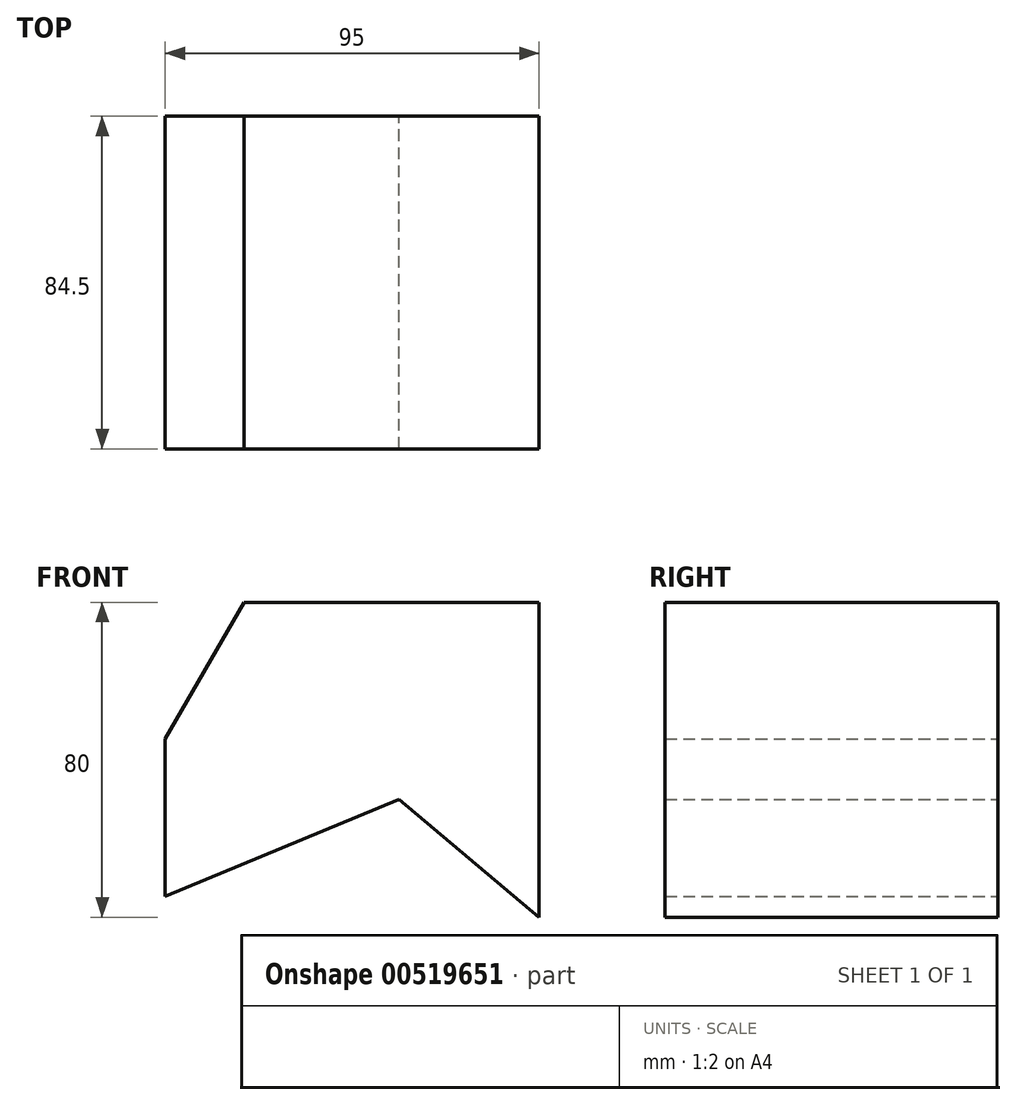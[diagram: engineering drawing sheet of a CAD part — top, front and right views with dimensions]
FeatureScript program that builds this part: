
annotation { "Feature Type Name" : "Feature", "Feature Type Description" : "" }
export const myFeature = defineFeature(function(context is Context, id is Id, definition is map)
    precondition{}
    {
        {
            var Q0;
            Q0=qCreatedBy(makeId("Front.planeOp"),FACE);
            var sketch = newSketch(context, id + "F0", { "sketchPlane" : qUnion([Q0])});
            skLineSegment(sketch, "E0", {"start": v(-39.33, 50.07) * mm, "end": v(35.67, 50.07) * mm});
            skLineSegment(sketch, "E1", {"start": v(35.67, 50.07) * mm, "end": v(35.67, -29.93) * mm});
            skLineSegment(sketch, "E2", {"start": v(35.67, -29.93) * mm, "end": v(0, 0) * mm});
            skLineSegment(sketch, "E3", {"start": v(0, 0) * mm, "end": v(-59.33, -24.57) * mm});
            skLineSegment(sketch, "E4", {"start": v(-59.33, -24.57) * mm, "end": v(-59.33, 15.43) * mm});
            skLineSegment(sketch, "E5", {"start": v(-59.33, 15.43) * mm, "end": v(-39.33, 50.07) * mm});
            skSolve(sketch);
        }
        {
            var Q0;
            Q0 = qSketchRegion(id + "F0", true);
            extrude(context, id + "F1", {"entities" : qUnion([Q0]), "depth" : 84.5 * mm, "offsetDistance" : 25 * mm});
        }
    });
